FCSTD DOCUMENT  (FreeCAD 0.19R0.19.2)
Label: 009
License: All rights reserved
LicenseURL: http://en.wikipedia.org/wiki/All_rights_reserved
objects: Sketcher::SketchObject×1
note: 1 computed .brp shape members not serialized (recipe doc carries the construction recipe); baked Part::Feature solids carry a one-line shape summary decoded from their .brp

FEATURE [Sketcher::SketchObject] Sketch
  FullyConstrained = false
  sketch-geometry (50):
    g0: ArcOfCircle CenterX=-3.45031e-07 CenterY=0 CenterZ=0 NormalX=0 NormalY=0 NormalZ=1 AngleXU=0 Radius=10.2 StartAngle=5.4126 EndAngle=7.15377
    g1: ArcOfCircle CenterX=-3.45031e-07 CenterY=0 CenterZ=0 NormalX=0 NormalY=0 NormalZ=1 AngleXU=0 Radius=10.2 StartAngle=2.27101 EndAngle=4.01218
    g2: LineSegment StartX=-6.57267 StartY=7.8 StartZ=0 EndX=6.57267 EndY=7.8 EndZ=0
    g3: LineSegment StartX=-6.57267 StartY=-7.8 StartZ=0 EndX=6.57267 EndY=-7.8 EndZ=0
    g4: ArcOfCircle CenterX=-3.45031e-07 CenterY=0 CenterZ=0 NormalX=0 NormalY=0 NormalZ=1 AngleXU=0 Radius=11.6 StartAngle=2.27101 EndAngle=2.66709
    g5: ArcOfCircle CenterX=-3.45031e-07 CenterY=0 CenterZ=0 NormalX=0 NormalY=0 NormalZ=1 AngleXU=0 Radius=11.6 StartAngle=5.4126 EndAngle=5.80868
    g6: LineSegment StartX=-7.4748 StartY=8.87059 StartZ=0 EndX=7.4748 EndY=8.87059 EndZ=0
    g7: LineSegment StartX=-7.4748 StartY=-8.87059 StartZ=0 EndX=7.4748 EndY=-8.87059 EndZ=0
    g8: LineSegment StartX=-11.3274 StartY=2.5 StartZ=0 EndX=-30.2 EndY=2.5 EndZ=0
    g9: LineSegment StartX=-11.3274 StartY=-2.5 StartZ=0 EndX=-30.2 EndY=-2.5 EndZ=0
    g10: LineSegment StartX=11.3274 StartY=2.5 StartZ=0 EndX=30.2 EndY=2.5 EndZ=0
    g11: LineSegment StartX=11.3274 StartY=-2.5 StartZ=0 EndX=30.2 EndY=-2.5 EndZ=0
    g12: LineSegment StartX=-30.2 StartY=2.5 StartZ=0 EndX=-30.2 EndY=3.5 EndZ=0
    g13: LineSegment StartX=30.2 StartY=2.5 StartZ=0 EndX=30.2 EndY=3.5 EndZ=0
    g14: LineSegment StartX=-30.2 StartY=-2.5 StartZ=0 EndX=-30.2 EndY=-3.5 EndZ=0
    g15: LineSegment StartX=30.2 StartY=-2.5 StartZ=0 EndX=30.2 EndY=-3.5 EndZ=0
    g16: LineSegment StartX=-30.2 StartY=3.5 StartZ=0 EndX=-28.8 EndY=3.5 EndZ=0
    g17: LineSegment StartX=-30.2 StartY=-3.5 StartZ=0 EndX=-28.8 EndY=-3.5 EndZ=0
    g18: LineSegment StartX=30.2 StartY=3.5 StartZ=0 EndX=28.8 EndY=3.5 EndZ=0
    g19: LineSegment StartX=30.2 StartY=-3.5 StartZ=0 EndX=28.8 EndY=-3.5 EndZ=0
    g20: ArcOfCircle CenterX=-3.45031e-07 CenterY=0 CenterZ=0 NormalX=0 NormalY=0 NormalZ=1 AngleXU=0 Radius=11.6 StartAngle=3.6161 EndAngle=4.01218
    g21: ArcOfCircle CenterX=-3.45031e-07 CenterY=0 CenterZ=0 NormalX=0 NormalY=0 NormalZ=1 AngleXU=0 Radius=11.6 StartAngle=0.474503 EndAngle=0.870585
    g22: Circle CenterX=-28.8 CenterY=3.5 CenterZ=0 NormalX=0 NormalY=0 NormalZ=1 AngleXU=0 Radius=1
    g23: Circle CenterX=-10.9247 CenterY=3.9 CenterZ=0 NormalX=0 NormalY=0 NormalZ=1 AngleXU=0 Radius=1
    g24: Circle CenterX=-10.3184 CenterY=5.3 CenterZ=0 NormalX=0 NormalY=0 NormalZ=1 AngleXU=0 Radius=1
    g25: BSplineCurve PolesCount=3 KnotsCount=2 Degree=2 IsPeriodic=0
    g26: GeomPoint X=-28.8 Y=3.5 Z=0
    g27: GeomPoint X=-10.3184 Y=5.3 Z=0
    g28: Circle CenterX=28.8 CenterY=3.5 CenterZ=0 NormalX=0 NormalY=0 NormalZ=1 AngleXU=0 Radius=1
    g29: Circle CenterX=10.9247 CenterY=3.9 CenterZ=0 NormalX=0 NormalY=0 NormalZ=1 AngleXU=0 Radius=1
    g30: Circle CenterX=10.3184 CenterY=5.3 CenterZ=0 NormalX=0 NormalY=0 NormalZ=1 AngleXU=0 Radius=1
    g31: BSplineCurve PolesCount=3 KnotsCount=2 Degree=2 IsPeriodic=0
    g32: GeomPoint X=28.8 Y=3.5 Z=0
    g33: GeomPoint X=10.3184 Y=5.3 Z=0
    g34: Circle CenterX=-28.8 CenterY=-3.5 CenterZ=0 NormalX=0 NormalY=0 NormalZ=1 AngleXU=0 Radius=1
    g35: Circle CenterX=-10.9247 CenterY=-3.9 CenterZ=0 NormalX=0 NormalY=0 NormalZ=1 AngleXU=0 Radius=1
    g36: Circle CenterX=-10.3184 CenterY=-5.3 CenterZ=0 NormalX=0 NormalY=0 NormalZ=1 AngleXU=0 Radius=1
    g37: BSplineCurve PolesCount=3 KnotsCount=2 Degree=2 IsPeriodic=0
    g38: GeomPoint X=-28.8 Y=-3.5 Z=0
    g39: GeomPoint X=-10.3184 Y=-5.3 Z=0
    g40: Circle CenterX=28.8 CenterY=-3.5 CenterZ=0 NormalX=0 NormalY=0 NormalZ=1 AngleXU=0 Radius=1
    g41: Circle CenterX=10.9247 CenterY=-3.9 CenterZ=0 NormalX=0 NormalY=0 NormalZ=1 AngleXU=0 Radius=1
    g42: Circle CenterX=10.3184 CenterY=-5.3 CenterZ=0 NormalX=0 NormalY=0 NormalZ=1 AngleXU=0 Radius=1
    g43: BSplineCurve PolesCount=3 KnotsCount=2 Degree=2 IsPeriodic=0
    g44: GeomPoint X=28.8 Y=-3.5 Z=0
    g45: GeomPoint X=10.3184 Y=-5.3 Z=0
    g46: ArcOfCircle CenterX=-3.45031e-07 CenterY=5e-07 CenterZ=0 NormalX=0 NormalY=0 NormalZ=1 AngleXU=0 Radius=11.6 StartAngle=6.06596 EndAngle=6.50041
    g47: ArcOfCircle CenterX=-3.45031e-07 CenterY=5e-07 CenterZ=0 NormalX=0 NormalY=0 NormalZ=1 AngleXU=0 Radius=11.6 StartAngle=2.92437 EndAngle=3.35881
    g48: LineSegment StartX=-3.45031e-07 StartY=0 StartZ=0 EndX=-13.6764 EndY=0 EndZ=0
    g49: LineSegment StartX=-3.45031e-07 StartY=0 StartZ=0 EndX=12.6345 EndY=0 EndZ=0
  constraints (110):
    c: Block(g0)
    c: Equal(g0,g1)
    c: Coincident(g0,g1)
    c: Coincident(g2,g1)
    c: Coincident(g2,g0)
    c: Horizontal(g2)
    c: Coincident(g3,g1)
    c: Coincident(g3,g0)
    c: Horizontal(g3)
    c: Block(g2)
    c: Block(g3)
    c: Coincident(g4,g0)
    c: Coincident(g5,g0)
    c: Block(g5)
    c: Block(g4)
    c: Coincident(g6,g4)
    c: Coincident(g6,g21)
    c: Horizontal(g6)
    c: Coincident(g7,g20)
    c: Coincident(g7,g5)
    c: Horizontal(g7)
    c: Horizontal(g8)
    c: Horizontal(g9)
    c: Horizontal(g10)
    c: Horizontal(g11)
    c: Coincident(g12,g8)
    c: Vertical(g12)
    c: Distance(g12) = 1
    c: Coincident(g13,g10)
    c: Vertical(g13)
    c: Distance(g13) = 1
    c: Coincident(g14,g9)
    c: Distance(g14) = 1
    c: Perpendicular(g14,g9)
    c: Coincident(g15,g11)
    c: Vertical(g15)
    c: Distance(g15) = 1
    c: Coincident(g16,g12)
    c: Horizontal(g16)
    c: Distance(g16) = 1.4
    c: Horizontal(g17)
    c: Equal(g16,g17) = 1.4
    c: Coincident(g17,g14)
    c: Coincident(g18,g13)
    c: Horizontal(g18)
    c: Distance(g18) = 1.4
    c: Horizontal(g19)
    c: Equal(g18,g19) = 1.4
    c: Coincident(g19,g15)
    c: Equal(g4,g20)
    c: Coincident(g4,g20)
    c: Equal(g5,g21)
    c: Coincident(g5,g21)
    c: Block(g20)
    c: Block(g21)
    c: Coincident(g25,g16)
    c: Weight(g22) = 1
    c: Equal(g22,g23)
    c: Equal(g22,g24)
    c: Coincident(g25,g4)
    c: InternalAlignment(g22,g25)
    c: InternalAlignment(g23,g25)
    c: InternalAlignment(g24,g25)
    c: InternalAlignment(g26,g25)
    c: InternalAlignment(g27,g25)
    c: Coincident(g31,g18)
    c: Weight(g28) = 1
    c: Equal(g28,g29)
    c: Equal(g28,g30)
    c: Coincident(g31,g21)
    c: InternalAlignment(g28,g31)
    c: InternalAlignment(g29,g31)
    c: InternalAlignment(g30,g31)
    c: InternalAlignment(g32,g31)
    c: InternalAlignment(g33,g31)
    c: Coincident(g37,g17)
    c: Weight(g34) = 1
    c: Equal(g34,g35)
    c: Equal(g34,g36)
    c: Coincident(g37,g20)
    c: InternalAlignment(g34,g37)
    c: InternalAlignment(g35,g37)
    c: InternalAlignment(g36,g37)
    c: InternalAlignment(g38,g37)
    c: InternalAlignment(g39,g37)
    c: Coincident(g43,g19)
    c: Weight(g40) = 1
    c: Equal(g40,g41)
    c: Equal(g40,g42)
    c: Coincident(g43,g5)
    c: InternalAlignment(g40,g43)
    c: InternalAlignment(g41,g43)
    c: InternalAlignment(g42,g43)
    c: InternalAlignment(g44,g43)
    c: InternalAlignment(g45,g43)
    c: Block(g31)
    c: Block(g25)
    c: Block(g46)
    c: Block(g47)
    c: Block(g43)
    c: Block(g37)
    c: Coincident(g10,g46)
    c: Coincident(g11,g46)
    c: Coincident(g8,g47)
    c: Coincident(g9,g47)
    c: Coincident(g48,g0)
    c: PointOnObject(g48,g-1)
    c: Horizontal(g48)
    c: Coincident(g49,g0)
    c: Horizontal(g49)
